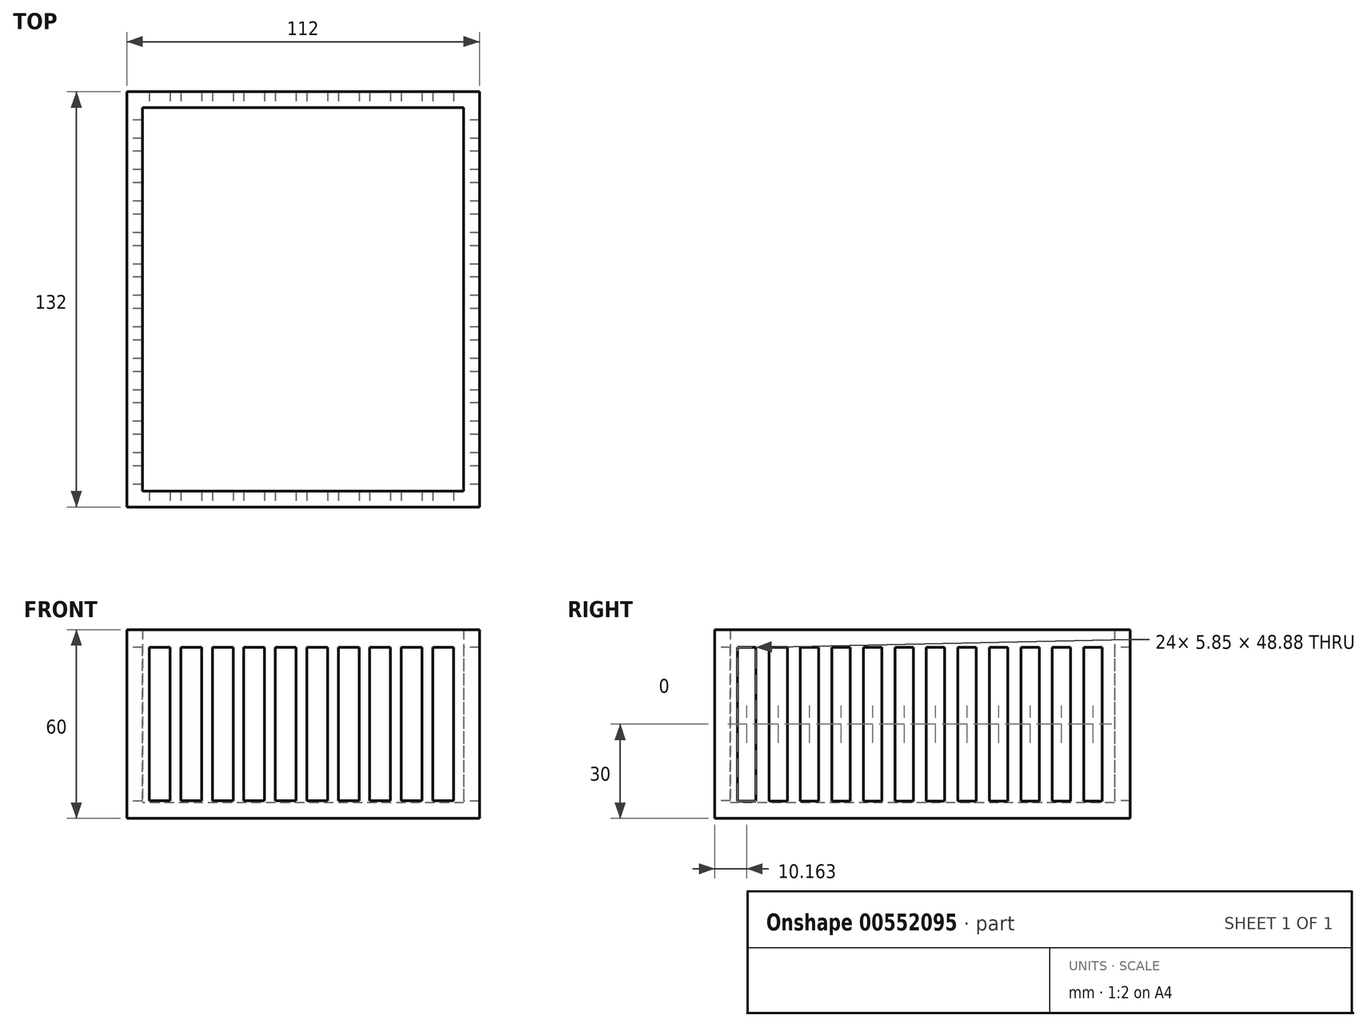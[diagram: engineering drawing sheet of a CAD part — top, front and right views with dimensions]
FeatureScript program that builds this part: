
annotation { "Feature Type Name" : "Feature", "Feature Type Description" : "" }
export const myFeature = defineFeature(function(context is Context, id is Id, definition is map)
    precondition{}
    {
        {
            var Q0;
            Q0=qCreatedBy(makeId("Top.planeOp"),FACE);
            var sketch = newSketch(context, id + "F0", { "sketchPlane" : qUnion([Q0])});
            skLineSegment(sketch, "E0.bottom", {"start": v(-54.48, 59.45) * mm, "end": v(45.52, 59.45) * mm});
            skLineSegment(sketch, "E0.top", {"start": v(-54.48, -60.55) * mm, "end": v(45.52, -60.55) * mm});
            skLineSegment(sketch, "E0.left", {"start": v(-54.48, 59.45) * mm, "end": v(-54.48, -60.55) * mm});
            skLineSegment(sketch, "E0.right", {"start": v(45.52, 59.45) * mm, "end": v(45.52, -60.55) * mm});
            skSolve(sketch);
        }
        {
            var Q0;
            Q0=makeQuery(id+"F0.imprint","IMPRINT",FACE,{"disambiguationData":[TD([[makeQuery(id+"F0.imprint","IMPRINT",EDGE,{"derivedFrom":sQuery(id+"F0.wireOp",EDGE,"E0.bottom")}),-1.0]])]});
            var sketch = newSketch(context, id + "F1", { "sketchPlane" : qUnion([Q0])});
            skLineSegment(sketch, "E1.0", {"start": v(-60.48, 65.45) * mm, "end": v(-60.48, -66.55) * mm});
            skLineSegment(sketch, "E1.1", {"start": v(51.52, 65.45) * mm, "end": v(-60.48, 65.45) * mm});
            skLineSegment(sketch, "E1.2", {"start": v(51.52, -66.55) * mm, "end": v(51.52, 65.45) * mm});
            skLineSegment(sketch, "E1.3", {"start": v(-60.48, -66.55) * mm, "end": v(51.52, -66.55) * mm});
            skSolve(sketch);
        }
        {
            var Q0;
            Q0 = qSketchRegion(id + "F1", true);
            extrude(context, id + "F2", {"entities" : qUnion([Q0]), "depth" : 5 * mm, "offsetDistance" : 25 * mm});
        }
        {
            var Q0;
            Q0=makeQuery(id+"F2.opExtrude","CAP_FACE",FACE,{"disambiguationData":[OSD([sQuery(id+"F1.wireOp",EDGE,"E1.0"),sQuery(id+"F1.wireOp",EDGE,"E1.1"),sQuery(id+"F1.wireOp",EDGE,"E1.2"),sQuery(id+"F1.wireOp",EDGE,"E1.3")])],"isStart":false});
            var sketch = newSketch(context, id + "F3", { "sketchPlane" : qUnion([Q0])});
            skLineSegment(sketch, "E2.0", {"start": v(-55.48, 60.45) * mm, "end": v(-55.48, -61.55) * mm});
            skLineSegment(sketch, "E2.1", {"start": v(46.52, 60.45) * mm, "end": v(-55.48, 60.45) * mm});
            skLineSegment(sketch, "E2.2", {"start": v(46.52, -61.55) * mm, "end": v(46.52, 60.45) * mm});
            skLineSegment(sketch, "E2.3", {"start": v(-55.48, -61.55) * mm, "end": v(46.52, -61.55) * mm});
            skSolve(sketch);
        }
        {
            var Q0;
            Q0=makeQuery(id+"F3.imprint","IMPRINT",FACE,{"disambiguationData":[TD([[makeQuery(id+"F3.imprint","IMPRINT",EDGE,{"derivedFrom":sQuery(id+"F3.wireOp",EDGE,"E2.0")}),-1.0]])]});
            extrude(context, id + "F4", {"entities" : qUnion([Q0]), "operationType" : NewBodyOperationType.ADD, "depth" : 55 * mm, "offsetDistance" : 25 * mm});
        }
        {
            var Q0;
            {var subQ0=sQuery(id+"F1.wireOp",EDGE,"E1.3");Q0=makeQuery(id+"F4.boolean.opBoolean","MERGE",FACE,{"derivedFrom":[makeQuery(id+"F2.opExtrude","SWEPT_FACE",FACE,{"disambiguationData":[OSD([subQ0])]}),makeQuery(id+"F4.opExtrude","SWEPT_FACE",FACE,{"disambiguationData":[OSD([subQ0])]})]});}
            var sketch = newSketch(context, id + "F5", { "sketchPlane" : qUnion([Q0])});
            skLineSegment(sketch, "E3", {"start": v(0, 0) * mm, "end": v(0, 60) * mm});
            skLineSegment(sketch, "E4.bottom", {"start": v(3.3, 54.36) * mm, "end": v(-3.3, 54.36) * mm});
            skLineSegment(sketch, "E4.top", {"start": v(3.3, 5.64) * mm, "end": v(-3.3, 5.64) * mm});
            skLineSegment(sketch, "E4.left", {"start": v(3.3, 54.36) * mm, "end": v(3.3, 5.64) * mm});
            skLineSegment(sketch, "E4.right", {"start": v(-3.3, 54.36) * mm, "end": v(-3.3, 5.64) * mm});
            skPoint(sketch, "E4.middle", {"position": v(0, 30) * mm});
            skLineSegment(sketch, "E5.1.0.0", {"start": v(13.3, 54.36) * mm, "end": v(13.3, 5.64) * mm});
            skLineSegment(sketch, "E5.1.0.1", {"start": v(13.3, 54.36) * mm, "end": v(6.7, 54.36) * mm});
            skLineSegment(sketch, "E5.1.0.2", {"start": v(6.7, 54.36) * mm, "end": v(6.7, 5.64) * mm});
            skLineSegment(sketch, "E5.1.0.3", {"start": v(13.3, 5.64) * mm, "end": v(6.7, 5.64) * mm});
            skLineSegment(sketch, "E5.2.0.0", {"start": v(23.3, 54.36) * mm, "end": v(23.3, 5.64) * mm});
            skLineSegment(sketch, "E5.2.0.1", {"start": v(23.3, 54.36) * mm, "end": v(16.7, 54.36) * mm});
            skLineSegment(sketch, "E5.2.0.2", {"start": v(16.7, 54.36) * mm, "end": v(16.7, 5.64) * mm});
            skLineSegment(sketch, "E5.2.0.3", {"start": v(23.3, 5.64) * mm, "end": v(16.7, 5.64) * mm});
            skLineSegment(sketch, "E5.3.0.0", {"start": v(33.3, 54.36) * mm, "end": v(33.3, 5.64) * mm});
            skLineSegment(sketch, "E5.3.0.1", {"start": v(33.3, 54.36) * mm, "end": v(26.7, 54.36) * mm});
            skLineSegment(sketch, "E5.3.0.2", {"start": v(26.7, 54.36) * mm, "end": v(26.7, 5.64) * mm});
            skLineSegment(sketch, "E5.3.0.3", {"start": v(33.3, 5.64) * mm, "end": v(26.7, 5.64) * mm});
            skLineSegment(sketch, "E5.4.0.0", {"start": v(43.3, 54.36) * mm, "end": v(43.3, 5.64) * mm});
            skLineSegment(sketch, "E5.4.0.1", {"start": v(43.3, 54.36) * mm, "end": v(36.7, 54.36) * mm});
            skLineSegment(sketch, "E5.4.0.2", {"start": v(36.7, 54.36) * mm, "end": v(36.7, 5.64) * mm});
            skLineSegment(sketch, "E5.4.0.3", {"start": v(43.3, 5.64) * mm, "end": v(36.7, 5.64) * mm});
            skLineSegment(sketch, "E5.direction1", {"start": v(3.3, 5.64) * mm, "end": v(13.3, 5.64) * mm, "construction": true});
            skLineSegment(sketch, "E6.1.0.0", {"start": v(-13.3, 54.36) * mm, "end": v(-13.3, 5.64) * mm});
            skLineSegment(sketch, "E6.1.0.1", {"start": v(-6.7, 54.36) * mm, "end": v(-13.3, 54.36) * mm});
            skLineSegment(sketch, "E6.1.0.2", {"start": v(-6.7, 5.64) * mm, "end": v(-13.3, 5.64) * mm});
            skLineSegment(sketch, "E6.1.0.3", {"start": v(-6.7, 54.36) * mm, "end": v(-6.7, 5.64) * mm});
            skLineSegment(sketch, "E6.2.0.0", {"start": v(-23.3, 54.36) * mm, "end": v(-23.3, 5.64) * mm});
            skLineSegment(sketch, "E6.2.0.1", {"start": v(-16.7, 54.36) * mm, "end": v(-23.3, 54.36) * mm});
            skLineSegment(sketch, "E6.2.0.2", {"start": v(-16.7, 5.64) * mm, "end": v(-23.3, 5.64) * mm});
            skLineSegment(sketch, "E6.2.0.3", {"start": v(-16.7, 54.36) * mm, "end": v(-16.7, 5.64) * mm});
            skLineSegment(sketch, "E6.3.0.0", {"start": v(-33.3, 54.36) * mm, "end": v(-33.3, 5.64) * mm});
            skLineSegment(sketch, "E6.3.0.1", {"start": v(-26.7, 54.36) * mm, "end": v(-33.3, 54.36) * mm});
            skLineSegment(sketch, "E6.3.0.2", {"start": v(-26.7, 5.64) * mm, "end": v(-33.3, 5.64) * mm});
            skLineSegment(sketch, "E6.3.0.3", {"start": v(-26.7, 54.36) * mm, "end": v(-26.7, 5.64) * mm});
            skLineSegment(sketch, "E6.4.0.0", {"start": v(-43.3, 54.36) * mm, "end": v(-43.3, 5.64) * mm});
            skLineSegment(sketch, "E6.4.0.1", {"start": v(-36.7, 54.36) * mm, "end": v(-43.3, 54.36) * mm});
            skLineSegment(sketch, "E6.4.0.2", {"start": v(-36.7, 5.64) * mm, "end": v(-43.3, 5.64) * mm});
            skLineSegment(sketch, "E6.4.0.3", {"start": v(-36.7, 54.36) * mm, "end": v(-36.7, 5.64) * mm});
            skLineSegment(sketch, "E6.5.0.0", {"start": v(-53.3, 54.36) * mm, "end": v(-53.3, 5.64) * mm});
            skLineSegment(sketch, "E6.5.0.1", {"start": v(-46.7, 54.36) * mm, "end": v(-53.3, 54.36) * mm});
            skLineSegment(sketch, "E6.5.0.2", {"start": v(-46.7, 5.64) * mm, "end": v(-53.3, 5.64) * mm});
            skLineSegment(sketch, "E6.5.0.3", {"start": v(-46.7, 54.36) * mm, "end": v(-46.7, 5.64) * mm});
            skLineSegment(sketch, "E6.direction1", {"start": v(-3.3, 5.64) * mm, "end": v(-13.3, 5.64) * mm, "construction": true});
            skSolve(sketch);
        }
        {
            var Q0;
            Q0 = qSketchRegion(id + "F5", true);
            extrude(context, id + "F6", {"entities" : qUnion([Q0]), "operationType" : NewBodyOperationType.REMOVE, "oppositeDirection" : true, "depth" : 200 * mm, "offsetDistance" : 25 * mm});
        }
        {
            var Q0;
            {var subQ0=sQuery(id+"F1.wireOp",EDGE,"E1.0");Q0=makeQuery(id+"F4.boolean.opBoolean","MERGE",FACE,{"derivedFrom":[makeQuery(id+"F2.opExtrude","SWEPT_FACE",FACE,{"disambiguationData":[OSD([subQ0])]}),makeQuery(id+"F4.opExtrude","SWEPT_FACE",FACE,{"disambiguationData":[OSD([subQ0])]})]});}
            var sketch = newSketch(context, id + "F7", { "sketchPlane" : qUnion([Q0])});
            skLineSegment(sketch, "E7", {"start": v(-65.45, 0) * mm, "end": v(-53.61, 0) * mm});
            skLineSegment(sketch, "E8", {"start": v(-53.61, 0) * mm, "end": v(-53.61, 60) * mm});
            skLineSegment(sketch, "E9.bottom", {"start": v(-50.69, 54.44) * mm, "end": v(-56.54, 54.44) * mm});
            skLineSegment(sketch, "E9.top", {"start": v(-50.69, 5.56) * mm, "end": v(-56.54, 5.56) * mm});
            skLineSegment(sketch, "E9.left", {"start": v(-50.69, 54.44) * mm, "end": v(-50.69, 5.56) * mm});
            skLineSegment(sketch, "E9.right", {"start": v(-56.54, 54.44) * mm, "end": v(-56.54, 5.56) * mm});
            skPoint(sketch, "E9.middle", {"position": v(-53.61, 30) * mm});
            skLineSegment(sketch, "E10.1.0.0", {"start": v(-40.69, 54.44) * mm, "end": v(-40.69, 5.56) * mm});
            skLineSegment(sketch, "E10.1.0.1", {"start": v(-46.54, 54.44) * mm, "end": v(-46.54, 5.56) * mm});
            skLineSegment(sketch, "E10.1.0.2", {"start": v(-40.69, 54.44) * mm, "end": v(-46.54, 54.44) * mm});
            skLineSegment(sketch, "E10.1.0.3", {"start": v(-40.69, 5.56) * mm, "end": v(-46.54, 5.56) * mm});
            skLineSegment(sketch, "E10.2.0.0", {"start": v(-30.69, 54.44) * mm, "end": v(-30.69, 5.56) * mm});
            skLineSegment(sketch, "E10.2.0.1", {"start": v(-36.54, 54.44) * mm, "end": v(-36.54, 5.56) * mm});
            skLineSegment(sketch, "E10.2.0.2", {"start": v(-30.69, 54.44) * mm, "end": v(-36.54, 54.44) * mm});
            skLineSegment(sketch, "E10.2.0.3", {"start": v(-30.69, 5.56) * mm, "end": v(-36.54, 5.56) * mm});
            skLineSegment(sketch, "E10.3.0.0", {"start": v(-20.69, 54.44) * mm, "end": v(-20.69, 5.56) * mm});
            skLineSegment(sketch, "E10.3.0.1", {"start": v(-26.54, 54.44) * mm, "end": v(-26.54, 5.56) * mm});
            skLineSegment(sketch, "E10.3.0.2", {"start": v(-20.69, 54.44) * mm, "end": v(-26.54, 54.44) * mm});
            skLineSegment(sketch, "E10.3.0.3", {"start": v(-20.69, 5.56) * mm, "end": v(-26.54, 5.56) * mm});
            skLineSegment(sketch, "E10.4.0.0", {"start": v(-10.69, 54.44) * mm, "end": v(-10.69, 5.56) * mm});
            skLineSegment(sketch, "E10.4.0.1", {"start": v(-16.54, 54.44) * mm, "end": v(-16.54, 5.56) * mm});
            skLineSegment(sketch, "E10.4.0.2", {"start": v(-10.69, 54.44) * mm, "end": v(-16.54, 54.44) * mm});
            skLineSegment(sketch, "E10.4.0.3", {"start": v(-10.69, 5.56) * mm, "end": v(-16.54, 5.56) * mm});
            skLineSegment(sketch, "E10.5.0.0", {"start": v(-0.69, 54.44) * mm, "end": v(-0.69, 5.56) * mm});
            skLineSegment(sketch, "E10.5.0.1", {"start": v(-6.54, 54.44) * mm, "end": v(-6.54, 5.56) * mm});
            skLineSegment(sketch, "E10.5.0.2", {"start": v(-0.69, 54.44) * mm, "end": v(-6.54, 54.44) * mm});
            skLineSegment(sketch, "E10.5.0.3", {"start": v(-0.69, 5.56) * mm, "end": v(-6.54, 5.56) * mm});
            skLineSegment(sketch, "E10.6.0.0", {"start": v(9.31, 54.44) * mm, "end": v(9.31, 5.56) * mm});
            skLineSegment(sketch, "E10.6.0.1", {"start": v(3.46, 54.44) * mm, "end": v(3.46, 5.56) * mm});
            skLineSegment(sketch, "E10.6.0.2", {"start": v(9.31, 54.44) * mm, "end": v(3.46, 54.44) * mm});
            skLineSegment(sketch, "E10.6.0.3", {"start": v(9.31, 5.56) * mm, "end": v(3.46, 5.56) * mm});
            skLineSegment(sketch, "E10.7.0.0", {"start": v(19.31, 54.44) * mm, "end": v(19.31, 5.56) * mm});
            skLineSegment(sketch, "E10.7.0.1", {"start": v(13.46, 54.44) * mm, "end": v(13.46, 5.56) * mm});
            skLineSegment(sketch, "E10.7.0.2", {"start": v(19.31, 54.44) * mm, "end": v(13.46, 54.44) * mm});
            skLineSegment(sketch, "E10.7.0.3", {"start": v(19.31, 5.56) * mm, "end": v(13.46, 5.56) * mm});
            skLineSegment(sketch, "E10.8.0.0", {"start": v(29.31, 54.44) * mm, "end": v(29.31, 5.56) * mm});
            skLineSegment(sketch, "E10.8.0.1", {"start": v(23.46, 54.44) * mm, "end": v(23.46, 5.56) * mm});
            skLineSegment(sketch, "E10.8.0.2", {"start": v(29.31, 54.44) * mm, "end": v(23.46, 54.44) * mm});
            skLineSegment(sketch, "E10.8.0.3", {"start": v(29.31, 5.56) * mm, "end": v(23.46, 5.56) * mm});
            skLineSegment(sketch, "E10.9.0.0", {"start": v(39.31, 54.44) * mm, "end": v(39.31, 5.56) * mm});
            skLineSegment(sketch, "E10.9.0.1", {"start": v(33.46, 54.44) * mm, "end": v(33.46, 5.56) * mm});
            skLineSegment(sketch, "E10.9.0.2", {"start": v(39.31, 54.44) * mm, "end": v(33.46, 54.44) * mm});
            skLineSegment(sketch, "E10.9.0.3", {"start": v(39.31, 5.56) * mm, "end": v(33.46, 5.56) * mm});
            skLineSegment(sketch, "E10.10.0.0", {"start": v(49.31, 54.44) * mm, "end": v(49.31, 5.56) * mm});
            skLineSegment(sketch, "E10.10.0.1", {"start": v(43.46, 54.44) * mm, "end": v(43.46, 5.56) * mm});
            skLineSegment(sketch, "E10.10.0.2", {"start": v(49.31, 54.44) * mm, "end": v(43.46, 54.44) * mm});
            skLineSegment(sketch, "E10.10.0.3", {"start": v(49.31, 5.56) * mm, "end": v(43.46, 5.56) * mm});
            skLineSegment(sketch, "E10.11.0.0", {"start": v(59.31, 54.44) * mm, "end": v(59.31, 5.56) * mm});
            skLineSegment(sketch, "E10.11.0.1", {"start": v(53.46, 54.44) * mm, "end": v(53.46, 5.56) * mm});
            skLineSegment(sketch, "E10.11.0.2", {"start": v(59.31, 54.44) * mm, "end": v(53.46, 54.44) * mm});
            skLineSegment(sketch, "E10.11.0.3", {"start": v(59.31, 5.56) * mm, "end": v(53.46, 5.56) * mm});
            skLineSegment(sketch, "E10.direction1", {"start": v(-50.69, 5.56) * mm, "end": v(-40.69, 5.56) * mm, "construction": true});
            skSolve(sketch);
        }
        {
            var Q0;
            Q0 = qSketchRegion(id + "F7", true);
            extrude(context, id + "F8", {"entities" : qUnion([Q0]), "operationType" : NewBodyOperationType.REMOVE, "oppositeDirection" : true, "depth" : 200 * mm, "offsetDistance" : 25 * mm});
        }
    });
